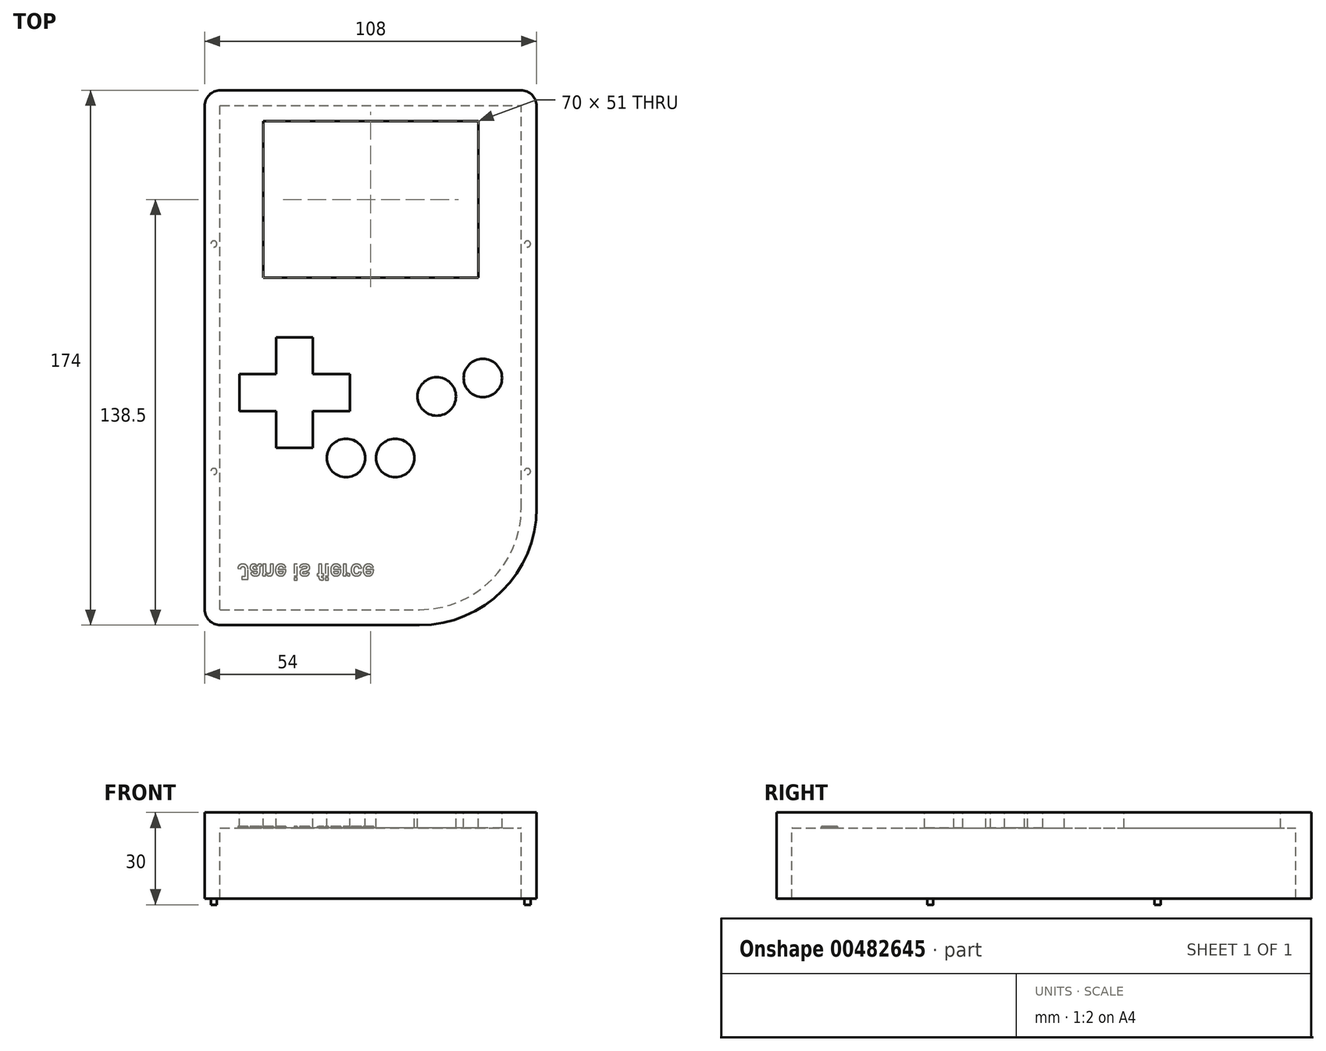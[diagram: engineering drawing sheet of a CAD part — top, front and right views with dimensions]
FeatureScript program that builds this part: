
annotation { "Feature Type Name" : "Feature", "Feature Type Description" : "" }
export const myFeature = defineFeature(function(context is Context, id is Id, definition is map)
    precondition{}
    {
        {
            var Q0;
            Q0=qCreatedBy(makeId("Top.planeOp"),FACE);
            var sketch = newSketch(context, id + "F0", { "sketchPlane" : qUnion([Q0])});
            skLineSegment(sketch, "E0.bottom", {"start": v(0, 0) * mm, "end": v(108, 0) * mm});
            skLineSegment(sketch, "E0.top", {"start": v(0, 174) * mm, "end": v(108, 174) * mm});
            skLineSegment(sketch, "E0.left", {"start": v(0, 0) * mm, "end": v(0, 174) * mm});
            skLineSegment(sketch, "E0.right", {"start": v(108, 0) * mm, "end": v(108, 174) * mm});
            skSolve(sketch);
        }
        {
            var Q0;
            Q0=makeQuery(id+"F0.imprint","IMPRINT",FACE,{"disambiguationData":[TD([[makeQuery(id+"F0.imprint","IMPRINT",EDGE,{"derivedFrom":sQuery(id+"F0.wireOp",EDGE,"E0.bottom")}),1.0]])]});
            extrude(context, id + "F1", {"entities" : qUnion([Q0]), "depth" : 28 * mm});
        }
        {
            var Q0;
            Q0=makeQuery(id+"F1.opExtrude","CAP_FACE",FACE,{"disambiguationData":[OSD([sQuery(id+"F0.wireOp",EDGE,"E0.bottom"),sQuery(id+"F0.wireOp",EDGE,"E0.top"),sQuery(id+"F0.wireOp",EDGE,"E0.left"),sQuery(id+"F0.wireOp",EDGE,"E0.right")])],"isStart":false});
            var sketch = newSketch(context, id + "F2", { "sketchPlane" : qUnion([Q0])});
            skLineSegment(sketch, "E1", {"start": v(54, 174) * mm, "end": v(54, 0) * mm, "construction": true});
            skLineSegment(sketch, "E2", {"start": v(25.09, 174) * mm, "end": v(25.09, 164) * mm, "construction": true});
            skLineSegment(sketch, "E3.bottom", {"start": v(19, 164) * mm, "end": v(89, 164) * mm});
            skLineSegment(sketch, "E3.top", {"start": v(19, 113) * mm, "end": v(89, 113) * mm});
            skLineSegment(sketch, "E3.left", {"start": v(19, 164) * mm, "end": v(19, 113) * mm});
            skLineSegment(sketch, "E3.right", {"start": v(89, 164) * mm, "end": v(89, 113) * mm});
            skLineSegment(sketch, "E4", {"start": v(0, 144.67) * mm, "end": v(19, 144.67) * mm, "construction": true});
            skLineSegment(sketch, "E5", {"start": v(89, 138.5) * mm, "end": v(108, 138.5) * mm, "construction": true});
            skLineSegment(sketch, "E6.bottom", {"start": v(11.25, 93.64) * mm, "end": v(47.25, 93.64) * mm, "construction": true});
            skLineSegment(sketch, "E6.top", {"start": v(11.25, 57.64) * mm, "end": v(47.25, 57.64) * mm, "construction": true});
            skLineSegment(sketch, "E6.left", {"start": v(11.25, 93.64) * mm, "end": v(11.25, 57.64) * mm, "construction": true});
            skLineSegment(sketch, "E6.right", {"start": v(47.25, 93.64) * mm, "end": v(47.25, 57.64) * mm, "construction": true});
            skLineSegment(sketch, "E7", {"start": v(11.25, 81.64) * mm, "end": v(23.25, 81.64) * mm});
            skLineSegment(sketch, "E8", {"start": v(23.25, 81.64) * mm, "end": v(23.25, 93.64) * mm});
            skLineSegment(sketch, "E9", {"start": v(35.25, 93.64) * mm, "end": v(35.25, 81.64) * mm});
            skLineSegment(sketch, "E10", {"start": v(35.25, 81.64) * mm, "end": v(47.25, 81.64) * mm});
            skLineSegment(sketch, "E11", {"start": v(47.25, 69.64) * mm, "end": v(35.25, 69.64) * mm});
            skLineSegment(sketch, "E12", {"start": v(35.25, 69.64) * mm, "end": v(35.25, 57.64) * mm});
            skLineSegment(sketch, "E13", {"start": v(11.25, 69.64) * mm, "end": v(23.25, 69.64) * mm});
            skLineSegment(sketch, "E14", {"start": v(23.25, 69.64) * mm, "end": v(23.25, 57.64) * mm});
            skCircle(sketch, "E15", {"center": v(90.5, 80.39) * mm, "radius": 6.25 * mm});
            skCircle(sketch, "E16", {"center": v(75.5, 74.39) * mm, "radius": 6.25 * mm});
            skCircle(sketch, "E17", {"center": v(46, 54.39) * mm, "radius": 6.25 * mm});
            skCircle(sketch, "E18", {"center": v(62, 54.39) * mm, "radius": 6.25 * mm});
            skLineSegment(sketch, "E19", {"start": v(46, 54.39) * mm, "end": v(0, 54.39) * mm, "construction": true});
            skLineSegment(sketch, "E20", {"start": v(62, 54.39) * mm, "end": v(108, 54.39) * mm, "construction": true});
            skLineSegment(sketch, "E21", {"start": v(23.25, 93.64) * mm, "end": v(35.25, 93.64) * mm});
            skLineSegment(sketch, "E22", {"start": v(47.25, 81.64) * mm, "end": v(47.25, 69.64) * mm});
            skLineSegment(sketch, "E23", {"start": v(35.25, 57.64) * mm, "end": v(23.25, 57.64) * mm});
            skLineSegment(sketch, "E24", {"start": v(11.25, 69.64) * mm, "end": v(11.25, 81.64) * mm});
            skLineSegment(sketch, "E25", {"start": v(69.25, 74.39) * mm, "end": v(47.25, 74.39) * mm, "construction": true});
            skLineSegment(sketch, "E26", {"start": v(75.5, 74.39) * mm, "end": v(69.25, 74.39) * mm, "construction": true});
            skLineSegment(sketch, "E27", {"start": v(62, 54.39) * mm, "end": v(62, 48.14) * mm, "construction": true});
            skLineSegment(sketch, "E28", {"start": v(62, 48.14) * mm, "end": v(75.5, 48.14) * mm, "construction": true});
            skLineSegment(sketch, "E29", {"start": v(75.5, 74.39) * mm, "end": v(75.5, 68.14) * mm, "construction": true});
            skLineSegment(sketch, "E30", {"start": v(75.5, 68.14) * mm, "end": v(75.5, 48.14) * mm, "construction": true});
            skLineSegment(sketch, "E31", {"start": v(46, 54.39) * mm, "end": v(39.75, 54.39) * mm, "construction": true});
            skSolve(sketch);
        }
        {
            var Q0;
            Q0=makeQuery(id+"F1.opExtrude","SWEPT_EDGE",EDGE,{"disambiguationData":[OSD([sQuery(id+"F0.wireOp",EDGE,"E0.bottom"),sQuery(id+"F0.wireOp",EDGE,"E0.right")])]});
            fillet(context, id + "F3", {"entities" : qUnion([Q0]), "radius" : 38.1 * mm, "tangentPropagation" : true, "allowEdgeOverflow" : false});
        }
        {
            var Q0;
            Q0=makeQuery(id+"F1.opExtrude","SWEPT_EDGE",EDGE,{"disambiguationData":[OSD([sQuery(id+"F0.wireOp",EDGE,"E0.bottom"),sQuery(id+"F0.wireOp",EDGE,"E0.left")])]});
            var Q1;
            Q1=makeQuery(id+"F1.opExtrude","SWEPT_EDGE",EDGE,{"disambiguationData":[OSD([sQuery(id+"F0.wireOp",EDGE,"E0.top"),sQuery(id+"F0.wireOp",EDGE,"E0.left")])]});
            var Q2;
            Q2=makeQuery(id+"F1.opExtrude","SWEPT_EDGE",EDGE,{"disambiguationData":[OSD([sQuery(id+"F0.wireOp",EDGE,"E0.top"),sQuery(id+"F0.wireOp",EDGE,"E0.right")])]});
            fillet(context, id + "F4", {"entities" : qUnion([Q0, Q1, Q2]), "radius" : 5.08 * mm, "tangentPropagation" : true, "allowEdgeOverflow" : false});
        }
        {
            var Q0;
            Q0=makeQuery(id+"F1.opExtrude","CAP_FACE",FACE,{"disambiguationData":[OSD([sQuery(id+"F0.wireOp",EDGE,"E0.bottom"),sQuery(id+"F0.wireOp",EDGE,"E0.top"),sQuery(id+"F0.wireOp",EDGE,"E0.left"),sQuery(id+"F0.wireOp",EDGE,"E0.right")])],"isStart":true});
            shell(context, id + "F5", {"entities" : qUnion([Q0]), "thickness" : 5 * mm});
        }
        {
            var Q0;
            Q0=qSketchRegion(id+"F2",true);
            extrude(context, id + "F6", {"entities" : qUnion([Q0]), "operationType" : NewBodyOperationType.REMOVE, "endBound" : BoundingType.UP_TO_NEXT, "oppositeDirection" : true, "depth" : 25.4 * mm});
        }
        {
            var Q0;
            Q0=makeQuery(id+"F5.opShell","OFFSET_FACE",FACE,{"disambiguationData":[OSD([sQuery(id+"F0.wireOp",EDGE,"E0.bottom"),sQuery(id+"F0.wireOp",EDGE,"E0.top"),sQuery(id+"F0.wireOp",EDGE,"E0.left"),sQuery(id+"F0.wireOp",EDGE,"E0.right")])]});
            var sketch = newSketch(context, id + "F7", { "sketchPlane" : qUnion([Q0])});
            skText(sketch, "E32", { "text": "Jane is fierce", "fontName": "Arimo-Bold.ttf"});
            skPoint(sketch, "E33", {"position": v(93.3, -14.7) * mm});
            const initialGuessF7  = {"E32": [0.01065, -0.01976, 1, 0, 0.00506]};
            skSetInitialGuess(sketch, initialGuessF7);
            skSolve(sketch);
        }
        {
            var Q0;
            Q0=qSketchRegion(id+"F7",true);
            extrude(context, id + "F8", {"entities" : qUnion([Q0]), "operationType" : NewBodyOperationType.REMOVE, "oppositeDirection" : true, "depth" : .5 * mm});
        }
        {
            var Q0;
            Q0=makeQuery(id+"F0.imprint","IMPRINT",FACE,{"disambiguationData":[TD([[makeQuery(id+"F0.imprint","IMPRINT",EDGE,{"derivedFrom":sQuery(id+"F0.wireOp",EDGE,"E0.bottom")}),1.0]])]});
            var sketch = newSketch(context, id + "F9", { "sketchPlane" : qUnion([Q0])});
            skLineSegment(sketch, "E34.bottom", {"start": v(108, 174) * mm, "end": v(0, 174) * mm, "construction": true});
            skLineSegment(sketch, "E34.top", {"start": v(108, 0) * mm, "end": v(0, 0) * mm, "construction": true});
            skLineSegment(sketch, "E34.left", {"start": v(108, 174) * mm, "end": v(108, 0) * mm, "construction": true});
            skLineSegment(sketch, "E34.right", {"start": v(0, 174) * mm, "end": v(0, 0) * mm, "construction": true});
            skLineSegment(sketch, "E35", {"start": v(105, 174) * mm, "end": v(105, 124) * mm, "construction": true});
            skLineSegment(sketch, "E36", {"start": v(3, 174) * mm, "end": v(3, 124) * mm, "construction": true});
            skLineSegment(sketch, "E37", {"start": v(105, 0) * mm, "end": v(105, 50) * mm, "construction": true});
            skLineSegment(sketch, "E38", {"start": v(3, 0) * mm, "end": v(3, 50) * mm, "construction": true});
            skLineSegment(sketch, "E39", {"start": v(108, 159.53) * mm, "end": v(105, 159.53) * mm, "construction": true});
            skLineSegment(sketch, "E40", {"start": v(0, 155.67) * mm, "end": v(3, 155.67) * mm, "construction": true});
            skLineSegment(sketch, "E41", {"start": v(0, 31.8) * mm, "end": v(3, 31.8) * mm, "construction": true});
            skLineSegment(sketch, "E42", {"start": v(108, 37.66) * mm, "end": v(105, 37.66) * mm});
            skCircle(sketch, "E43", {"center": v(105, 50) * mm, "radius": 1 * mm});
            skCircle(sketch, "E44", {"center": v(3, 50) * mm, "radius": 1 * mm});
            skCircle(sketch, "E45", {"center": v(3, 124) * mm, "radius": 1 * mm});
            skCircle(sketch, "E46", {"center": v(105, 124) * mm, "radius": 1 * mm});
            skSolve(sketch);
        }
        {
            var Q0;
            Q0=qSketchRegion(id+"F9",true);
            extrude(context, id + "F10", {"entities" : qUnion([Q0]), "operationType" : NewBodyOperationType.ADD, "oppositeDirection" : true, "depth" : 2 * mm, "offsetDistance" : 25.4 * mm});
        }
    });
